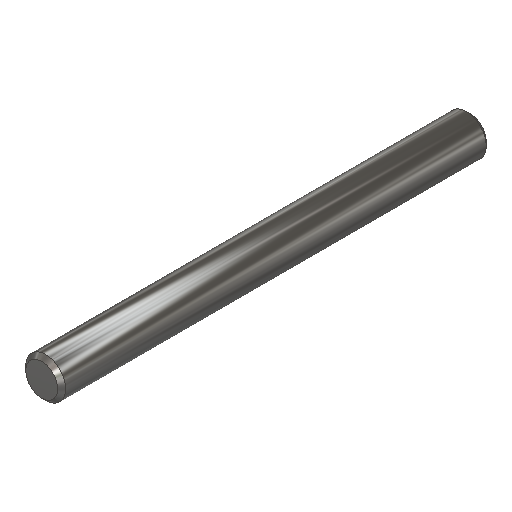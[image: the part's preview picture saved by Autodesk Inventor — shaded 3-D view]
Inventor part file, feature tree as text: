
AUTODESK INVENTOR PART (.ipt)
format: ipt  version: 2025 (Build 290162010, 162A)  size: 122,368 bytes
history: native  units: mm
features: extrude x1, chamfer x1
ambient origin geometry x8: Origin, YZ Plane, XZ Plane, XY Plane, X Axis, Y Axis, Z Axis, Center Point
bodies: Solid1 (feature_tree)
feature tree (2):
  extrude  "Extrusion1"  Depth=5.0mm
  chamfer  "Chamfer1"  Distance=53.5mm
